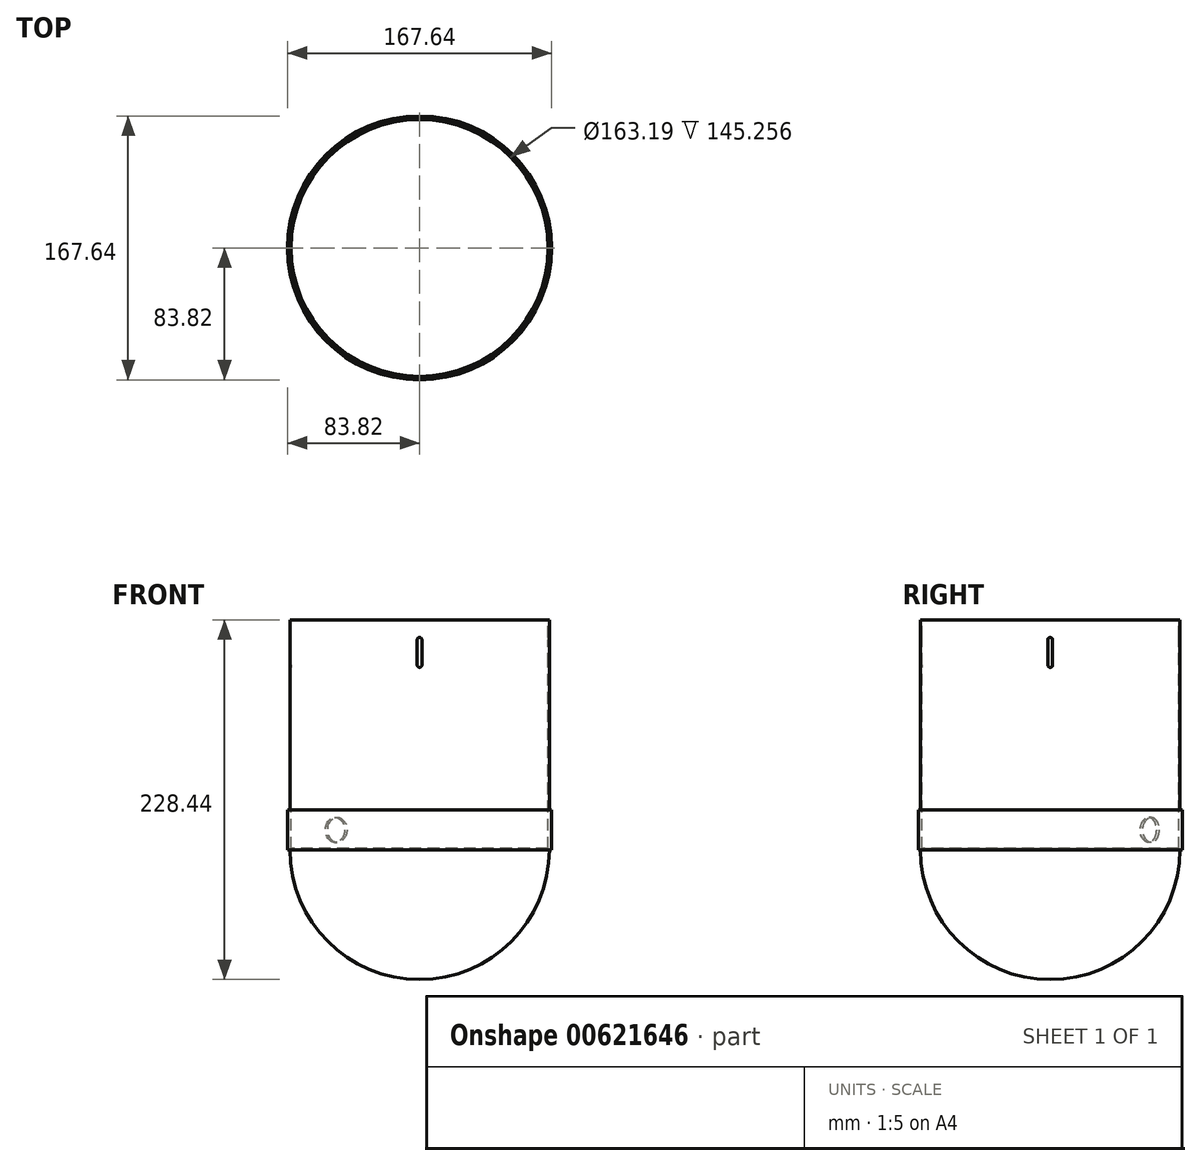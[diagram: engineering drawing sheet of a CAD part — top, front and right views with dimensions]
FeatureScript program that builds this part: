
annotation { "Feature Type Name" : "Feature", "Feature Type Description" : "" }
export const myFeature = defineFeature(function(context is Context, id is Id, definition is map)
    precondition{}
    {
        {
            var Q0;
            Q0=qCreatedBy(makeId("Top.planeOp"),FACE);
            var sketch = newSketch(context, id + "F0", { "sketchPlane" : qUnion([Q0])});
            skCircle(sketch, "E0", {"center": v(0, 0) * mm, "radius": 82.4 * mm});
            skSolve(sketch);
        }
        {
            var Q0;
            Q0=qSketchRegion(id+"F0",true);
            extrude(context, id + "F1", {"entities" : qUnion([Q0]), "oppositeDirection" : true, "depth" : 146.05 * mm, "offsetDistance" : 25.4 * mm});
        }
        {
            var Q0;
            Q0=makeQuery(id+"F1.opExtrude","CAP_FACE",FACE,{"disambiguationData":[OSD([sQuery(id+"F0.wireOp",EDGE,"E0")])],"isStart":true});
            shell(context, id + "F2", {"entities" : qUnion([Q0]), "thickness" : 0.8 * mm});
        }
        {
            var Q0;
            Q0=makeQuery(id+"F1.opExtrude","CAP_EDGE",EDGE,{"disambiguationData":[OSD([sQuery(id+"F0.wireOp",EDGE,"E0")])],"isStart":true});
            cPlane(context, id + "F3", {"entities" : qUnion([Q0]), "cplaneType" : CPlaneType.LINE_ANGLE, "offset" : 165.1 * mm, "angle" : 0 * degree, "width" : 152.4 * mm, "height" : 152.4 * mm});
        }
        {
            var Q0;
            Q0=qCreatedBy(id+"F3.planeOp",FACE);
            var sketch = newSketch(context, id + "F4", { "sketchPlane" : qUnion([Q0])});
            skLineSegment(sketch, "E1", {"start": v(0, 0) * mm, "end": v(32.57, 0) * mm, "construction": true});
            skLineSegment(sketch, "E2", {"start": v(0, 0) * mm, "end": v(-32.1, 0) * mm, "construction": true});
            skLineSegment(sketch, "E3", {"start": v(0, 0) * mm, "end": v(0, -28.58) * mm, "construction": true});
            skLineSegment(sketch, "E4.bottom", {"start": v(-1.52, -28.58) * mm, "end": v(1.52, -28.58) * mm});
            skLineSegment(sketch, "E4.top", {"start": v(-1.52, -12.7) * mm, "end": v(1.52, -12.7) * mm});
            skLineSegment(sketch, "E4.left", {"start": v(-1.52, -28.58) * mm, "end": v(-1.52, -12.7) * mm});
            skLineSegment(sketch, "E4.right", {"start": v(1.52, -28.58) * mm, "end": v(1.52, -12.7) * mm});
            skPoint(sketch, "E4.middle", {"position": v(0, -20.64) * mm});
            skArc(sketch, "E5", {"start": v(1.52, -12.7) * mm, "mid": v(0, -11.18) * mm, "end": v(-1.52, -12.7) * mm});
            skArc(sketch, "E6", {"start": v(-1.52, -28.58) * mm, "mid": v(0, -30.1) * mm, "end": v(1.52, -28.58) * mm});
            skSolve(sketch);
        }
        {
            var Q0;
            Q0=qSketchRegion(id+"F4",true);
            extrude(context, id + "F5", {"entities" : qUnion([Q0]), "operationType" : NewBodyOperationType.REMOVE, "oppositeDirection" : true, "depth" : 177.8 * mm, "offsetDistance" : 25.4 * mm, "symmetric" : true});
        }
        {
            var Q0;
            Q0=makeQuery(id+"F1.opExtrude","CAP_EDGE",EDGE,{"disambiguationData":[OSD([sQuery(id+"F0.wireOp",EDGE,"E0")])],"isStart":true});
            cPlane(context, id + "F6", {"entities" : qUnion([Q0]), "cplaneType" : CPlaneType.LINE_ANGLE, "offset" : 25.4 * mm, "angle" : 90 * degree, "width" : 152.4 * mm, "height" : 152.4 * mm});
        }
        {
            var Q0;
            Q0=qCreatedBy(id+"F6.planeOp",FACE);
            var sketch = newSketch(context, id + "F7", { "sketchPlane" : qUnion([Q0])});
            skLineSegment(sketch, "E7", {"start": v(71.83, 0) * mm, "end": v(-77.17, 0) * mm, "construction": true});
            skLineSegment(sketch, "E8", {"start": v(0, 0) * mm, "end": v(0, -95.04) * mm, "construction": true});
            skLineSegment(sketch, "E9.bottom", {"start": v(1.52, -28.58) * mm, "end": v(-1.52, -28.58) * mm});
            skLineSegment(sketch, "E9.top", {"start": v(1.52, -12.7) * mm, "end": v(-1.52, -12.7) * mm});
            skLineSegment(sketch, "E9.left", {"start": v(1.52, -28.58) * mm, "end": v(1.52, -12.7) * mm});
            skLineSegment(sketch, "E9.right", {"start": v(-1.52, -28.58) * mm, "end": v(-1.52, -12.7) * mm});
            skPoint(sketch, "E9.middle", {"position": v(0, -20.64) * mm});
            skArc(sketch, "E10", {"start": v(1.52, -12.7) * mm, "mid": v(0, -11.18) * mm, "end": v(-1.52, -12.7) * mm});
            skArc(sketch, "E11", {"start": v(-1.52, -28.58) * mm, "mid": v(0, -30.1) * mm, "end": v(1.52, -28.58) * mm});
            skSolve(sketch);
        }
        {
            var Q0;
            Q0=qSketchRegion(id+"F7",true);
            extrude(context, id + "F8", {"entities" : qUnion([Q0]), "operationType" : NewBodyOperationType.REMOVE, "oppositeDirection" : true, "depth" : 177.8 * mm, "offsetDistance" : 25.4 * mm, "symmetric" : true});
        }
        {
            var Q0;
            Q0=makeQuery(id+"F1.opExtrude","CAP_FACE",FACE,{"disambiguationData":[OSD([sQuery(id+"F0.wireOp",EDGE,"E0")])],"isStart":false});
            var sketch = newSketch(context, id + "F9", { "sketchPlane" : qUnion([Q0])});
            skCircle(sketch, "E12", {"center": v(0, 0) * mm, "radius": 83.82 * mm});
            skSolve(sketch);
        }
        {
            var Q0;
            Q0=makeQuery(id+"F9.imprint","IMPRINT",FACE,{"disambiguationData":[TD([[makeQuery(id+"F9.imprint","IMPRINT",EDGE,{"derivedFrom":sQuery(id+"F9.wireOp",EDGE,"E12")}),1.0]])]});
            extrude(context, id + "F10", {"entities" : qUnion([Q0]), "oppositeDirection" : true, "depth" : 25.4 * mm, "offsetDistance" : 25.4 * mm});
        }
        {
            var Q0;
            Q0=makeQuery(id+"F1.opExtrude","CAP_FACE",FACE,{"disambiguationData":[OSD([sQuery(id+"F0.wireOp",EDGE,"E0")])],"isStart":false});
            var sketch = newSketch(context, id + "F11", { "sketchPlane" : qUnion([Q0])});
            skLineSegment(sketch, "E13", {"start": v(0, -82.4) * mm, "end": v(0, 82.4) * mm, "construction": true});
            skLineSegment(sketch, "E14", {"start": v(0, 82.4) * mm, "end": v(0, -82.4) * mm});
            skSolve(sketch);
        }
        {
            var Q0;
            Q0=qSketchRegion(id+"F11",true);
            var Q1;
            {var subQ0=sQuery(id+"F11.wireOp",EDGE,"E14");Q1=makeQuery(id+"F11.imprint","IMPRINT",FACE,{"disambiguationData":[TD([[makeQuery(id+"F11.imprint","IMPRINT",EDGE,{"derivedFrom":subQ0}),-1.0]])]});}
            var Q2;
            Q2=sQuery(id+"F11.wireOp",EDGE,"E14");
            revolve(context, id + "F12", {"operationType" : NewBodyOperationType.ADD, "entities" : qUnion([Q0, Q1]), "axis" : qUnion([Q2]), "revolveType" : RevolveType.ONE_DIRECTION, "oppositeDirection" : true, "angle" : 180 * degree});
        }
        {
            var Q0;
            Q0=makeQuery(id+"F10.opExtrude","SWEPT_FACE",FACE,{"disambiguationData":[OSD([sQuery(id+"F9.wireOp",EDGE,"E12")])]});
            cPlane(context, id + "F13", {"entities" : qUnion([Q0]), "cplaneType" : CPlaneType.LINE_ANGLE, "offset" : 25.4 * mm, "angle" : 130 * degree, "oppositeDirection" : true, "width" : 152.4 * mm, "height" : 152.4 * mm});
        }
        {
            var Q0;
            Q0=qCreatedBy(id+"F13.planeOp",FACE);
            var sketch = newSketch(context, id + "F14", { "sketchPlane" : qUnion([Q0])});
            skLineSegment(sketch, "E15", {"start": v(0, 0) * mm, "end": v(0, -186.05) * mm, "construction": true});
            skLineSegment(sketch, "E16", {"start": v(-83.8, -120.64) * mm, "end": v(-83.8, -146.05) * mm, "construction": true});
            skLineSegment(sketch, "E17", {"start": v(-83.8, -133.34) * mm, "end": v(36.36, -133.34) * mm, "construction": true});
            skCircle(sketch, "E18", {"center": v(0, -133.34) * mm, "radius": 7.94 * mm});
            skSolve(sketch);
        }
        {
            var Q0;
            Q0 = qSketchRegion(id + "F14", true);
            extrude(context, id + "F15", {"entities" : qUnion([Q0]), "operationType" : NewBodyOperationType.REMOVE, "oppositeDirection" : true, "depth" : 88.9 * mm, "offsetDistance" : 25.4 * mm});
        }
    });
